# Revit family: РИДАН_Кран шаровой_RJIP Premium FF WG_PN16_DN350-600
name_source: partatom
category: Арматура трубопроводов
units: mm (PartAtom-declared; Revit-internal decimal feet)

## family parameters
Всегда вертикально = Да
На основе рабочей плоскости = Нет
Общий = Нет
При загрузке вырезать с полостями = Нет
Размер круглого соединителя = Использовать диаметр
Тип детали = Вставляется

## types (4) — shared parameters
ADSK_Версия Revit = 2019
ADSK_Версия семейства = 1.0
ADSK_Единица измерения = шт.
ADSK_Завод-изготовитель = ООО «Ридан-Трейд»
ADSK_Количество = 1
ADSK_Материал = <По категории>
ADSK_Потеря давления жидкости = 0.0 Па
ADSK_Расход жидкости = 0.0000 м³/ч
LT = R-JIP_PN16_1
URL = https://ridan.ru

## per-type parameters (varying)
- DN350: ADSK_Диаметр условный=350 мм; ADSK_Код изделия=065N0271GR; ADSK_Марка=RJIP Premium FF WG PN16 DN350; ADSK_Масса=396; ADSK_Наименование=Кран шаровой RJIP Premium фланцевый с ручным редукторным приводом PN16, Tmax=180C, DN350; ADSK_Пропускная способность=7560.0000 м³/ч; a=550 мм; b=458 мм; c=450 мм; d=377 мм; d1=189 мм; e=4 мм; f=38 мм; g=87 мм; h=46 мм; i=430 мм; j=215 мм; k=253 мм; l=331 мм; m=18 мм; n=210 мм; o=98 мм; p=381 мм; q=361 мм; r=127 мм; s=350 мм; t=371 мм; Редкутор_350_400=Да; Редуктор_500=Нет; Редуктор_600=Нет; УГО_Длина=780 мм
- DN400: ADSK_Диаметр условный=400 мм; ADSK_Код изделия=065N0276GR; ADSK_Марка=RJIP Premium FF WG PN16 DN400; ADSK_Масса=512; ADSK_Наименование=Кран шаровой RJIP Premium фланцевый с ручным редукторным приводом PN16, Tmax=180C, DN400; ADSK_Пропускная способность=10523.0000 м³/ч; a=610 мм; b=513 мм; c=505 мм; d=426 мм; d1=213 мм; e=4 мм; f=40 мм; g=108 мм; h=65 мм; i=462 мм; j=231 мм; k=278 мм; l=365 мм; m=18 мм; n=210 мм; o=124 мм; p=406 мм; q=386 мм; r=140 мм; s=500 мм; t=396 мм; Редкутор_350_400=Да; Редуктор_500=Нет; Редуктор_600=Нет; УГО_Длина=895 мм
- DN500: ADSK_Диаметр условный=500 мм; ADSK_Код изделия=065N0281GR; ADSK_Марка=RJIP Premium FF WG PN16 DN500; ADSK_Масса=880; ADSK_Наименование=Кран шаровой RJIP Premium фланцевый с ручным редукторным приводом PN16, Tmax=180C, DN500; ADSK_Пропускная способность=14258.0000 м³/ч; a=730 мм; b=623 мм; c=615 мм; d=520 мм; d1=260 мм; e=4 мм; f=48 мм; g=217 мм; h=94 мм; i=544 мм; j=272 мм; k=370 мм; l=457 мм; m=23 мм; n=300 мм; o=150 мм; p=518 мм; q=498 мм; r=159 мм; s=500 мм; t=508 мм; Редкутор_350_400=Нет; Редуктор_500=Да; Редуктор_600=Нет; УГО_Длина=1270 мм
- DN600: ADSK_Диаметр условный=600 мм; ADSK_Код изделия=065N0286GR; ADSK_Марка=RJIP Premium FF WG PN16 DN600; ADSK_Масса=1336; ADSK_Наименование=Кран шаровой RJIP Premium фланцевый с ручным редукторным приводом PN16, Tmax=180C, DN600; ADSK_Пропускная способность=22445.0000 м³/ч; a=840 мм; b=730 мм; c=720 мм; d=630 мм; d1=315 мм; e=5 мм; f=49 мм; g=146 мм; h=77 мм; i=609 мм; j=305 мм; k=404 мм; l=503 мм; m=28 мм; n=350 мм; o=165 мм; p=552 мм; q=532 мм; r=159 мм; s=500 мм; t=542 мм; Редкутор_350_400=Нет; Редуктор_500=Нет; Редуктор_600=Да; УГО_Длина=1163 мм
